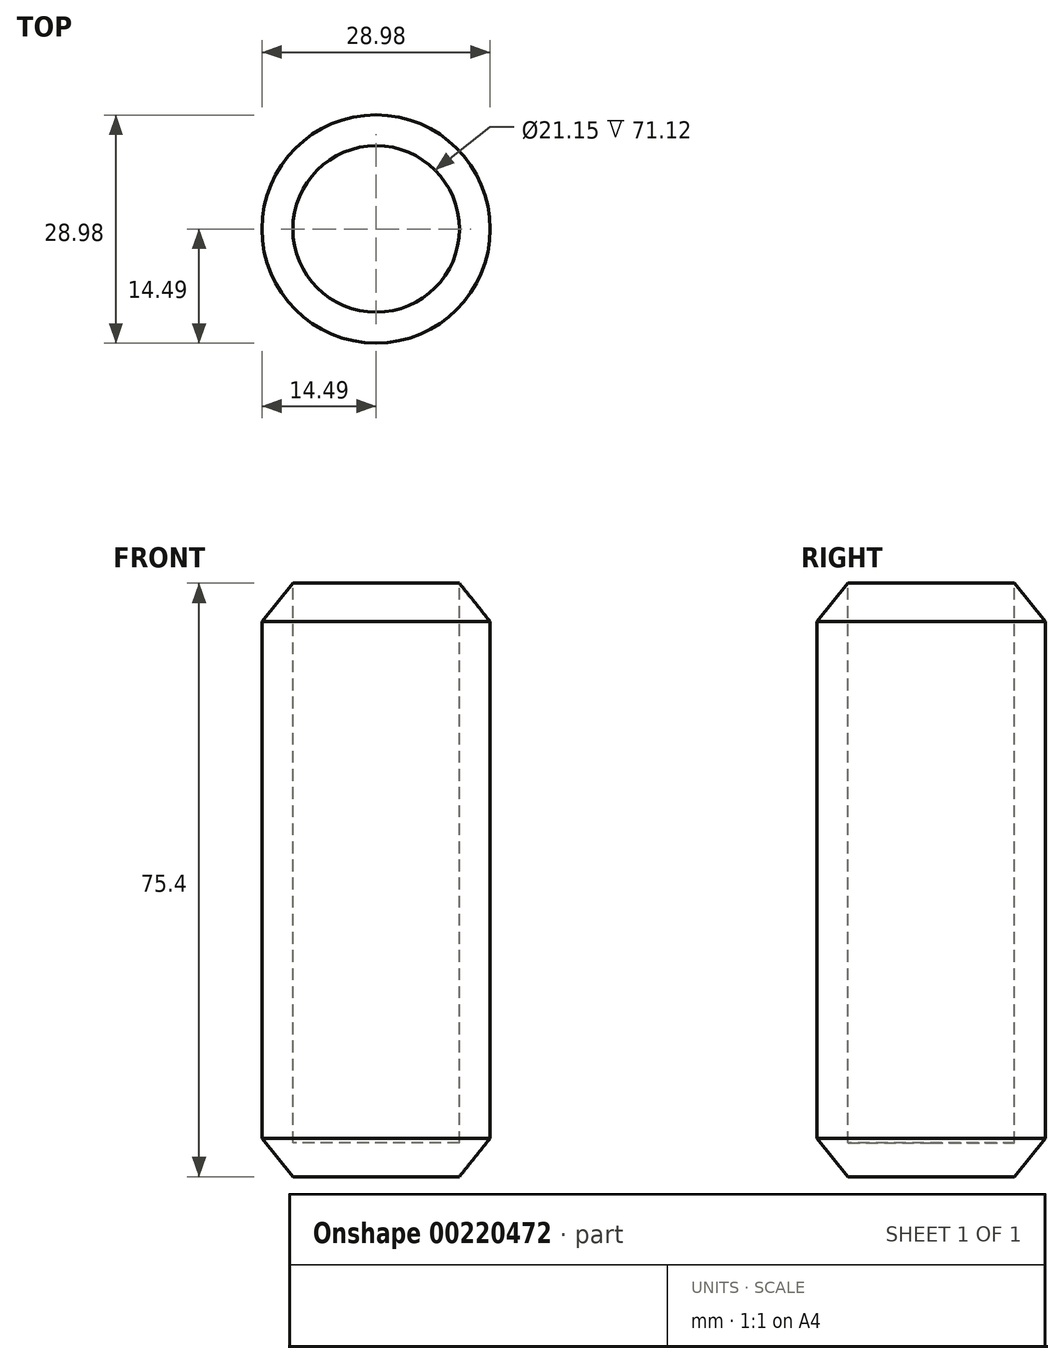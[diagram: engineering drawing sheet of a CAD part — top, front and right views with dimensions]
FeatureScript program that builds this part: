
annotation { "Feature Type Name" : "Feature", "Feature Type Description" : "" }
export const myFeature = defineFeature(function(context is Context, id is Id, definition is map)
    precondition{}
    {
        {
            var Q0;
            Q0=qCreatedBy(makeId("Front.planeOp"),FACE);
            var sketch = newSketch(context, id + "F0", { "sketchPlane" : qUnion([Q0])});
            skLineSegment(sketch, "E0.top", {"start": v(0, 37.7) * mm, "end": v(-10.58, 37.7) * mm});
            skLineSegment(sketch, "E0.left", {"start": v(0, 0) * mm, "end": v(0, 37.7) * mm});
            skLineSegment(sketch, "E0.right", {"start": v(-14.5, 0) * mm, "end": v(-14.5, 32.8) * mm});
            skLineSegment(sketch, "E1", {"start": v(-14.5, 32.8) * mm, "end": v(-10.58, 37.7) * mm});
            skLineSegment(sketch, "E2.MirrorCS", {"start": v(-14.5, 0) * mm, "end": v(-14.5, -32.8) * mm});
            skLineSegment(sketch, "E3.MirrorCS", {"start": v(-14.5, -32.8) * mm, "end": v(-10.58, -37.7) * mm});
            skLineSegment(sketch, "E4.MirrorCS", {"start": v(0, -37.7) * mm, "end": v(-10.58, -37.7) * mm});
            skLineSegment(sketch, "E5.MirrorCS", {"start": v(0, 0) * mm, "end": v(0, -37.7) * mm});
            skSolve(sketch);
        }
        {
            var Q0;
            Q0=makeQuery(id+"F0.imprint","IMPRINT",FACE,{"disambiguationData":[TD([[makeQuery(id+"F0.imprint","IMPRINT",EDGE,{"derivedFrom":sQuery(id+"F0.wireOp",EDGE,"E0.top")}),1.0]])]});
            var Q1;
            Q1=sQuery(id+"F0.wireOp",EDGE,"E5.MirrorCS");
            revolve(context, id + "F1", {"entities" : qUnion([Q0]), "axis" : qUnion([Q1]), "revolveType" : RevolveType.FULL});
        }
        {
            var Q0;
            Q0=makeQuery(id+"F1.opRevolve","SWEPT_FACE",FACE,{"disambiguationData":[OSD([sQuery(id+"F0.wireOp",EDGE,"E0.top")])]});
            var sketch = newSketch(context, id + "F2", { "sketchPlane" : qUnion([Q0])});
            skSolve(sketch);
        }
        {
            var Q0;
            Q0=makeQuery(id+"F2.imprint","IMPRINT",FACE,{"disambiguationData":[TD([[makeQuery(id+"F2.imprint","IMPRINT",EDGE,{"derivedFrom":makeQuery(id+"F1.opRevolve","SWEPT_EDGE",EDGE,{"disambiguationData":[OSD([sQuery(id+"F0.wireOp",EDGE,"E0.top"),sQuery(id+"F0.wireOp",EDGE,"E1")])]})}),1.0]])]});
            extrude(context, id + "F3", {"entities" : qUnion([Q0]), "operationType" : NewBodyOperationType.REMOVE, "oppositeDirection" : true, "depth" : 71.12 * mm});
        }
    });
